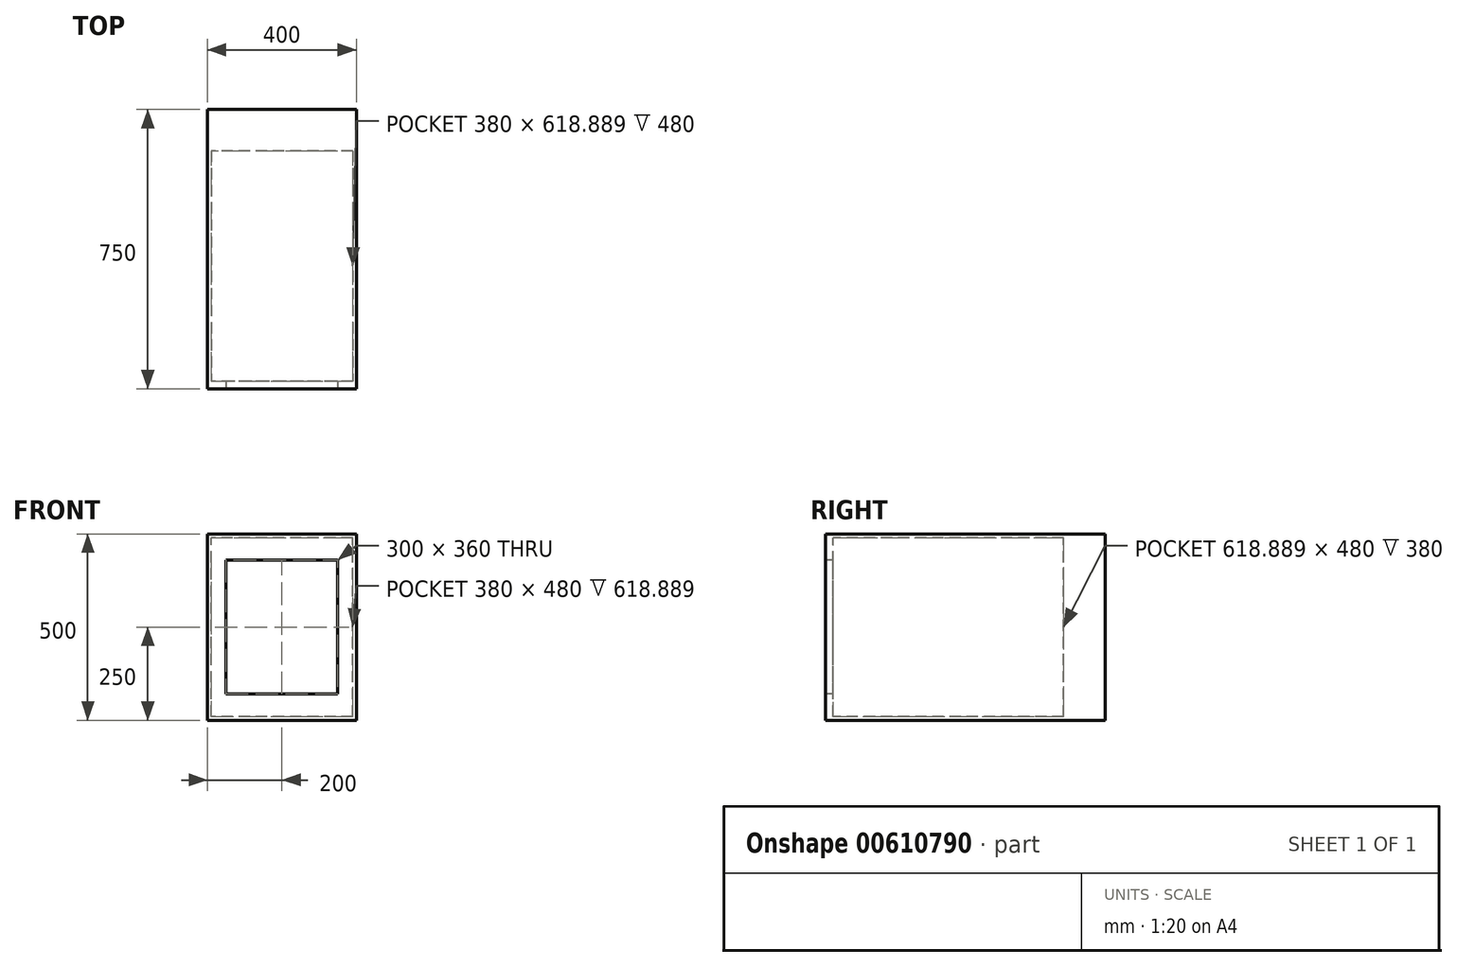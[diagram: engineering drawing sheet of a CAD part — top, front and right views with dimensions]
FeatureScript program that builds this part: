
annotation { "Feature Type Name" : "Feature", "Feature Type Description" : "" }
export const myFeature = defineFeature(function(context is Context, id is Id, definition is map)
    precondition{}
    {
        {
            var Q0;
            Q0=qCreatedBy(makeId("Front.planeOp"),FACE);
            var sketch = newSketch(context, id + "F0", { "sketchPlane" : qUnion([Q0])});
            skLineSegment(sketch, "E0.bottom", {"start": v(0, 0) * mm, "end": v(400, 0) * mm});
            skLineSegment(sketch, "E0.top", {"start": v(0, 500) * mm, "end": v(400, 500) * mm});
            skLineSegment(sketch, "E0.left", {"start": v(0, 0) * mm, "end": v(0, 500) * mm});
            skLineSegment(sketch, "E0.right", {"start": v(400, 0) * mm, "end": v(400, 500) * mm});
            skSolve(sketch);
        }
        {
            var Q0;
            Q0=qSketchRegion(id+"F0",true);
            extrude(context, id + "F1", {"entities" : qUnion([Q0]), "depth" : 750 * mm, "offsetDistance" : 25 * mm});
        }
        {
            var Q0;
            Q0=makeQuery(id+"F1.opExtrude","CAP_FACE",FACE,{"disambiguationData":[OSD([sQuery(id+"F0.wireOp",EDGE,"E0.bottom"),sQuery(id+"F0.wireOp",EDGE,"E0.top"),sQuery(id+"F0.wireOp",EDGE,"E0.left"),sQuery(id+"F0.wireOp",EDGE,"E0.right")])],"isStart":false});
            var sketch = newSketch(context, id + "F2", { "sketchPlane" : qUnion([Q0])});
            skLineSegment(sketch, "E1", {"start": v(0, 0) * mm, "end": v(400, 500) * mm});
            skLineSegment(sketch, "E2.bottom", {"start": v(350, 70) * mm, "end": v(50, 70) * mm});
            skLineSegment(sketch, "E2.top", {"start": v(350, 430) * mm, "end": v(50, 430) * mm});
            skLineSegment(sketch, "E2.left", {"start": v(350, 70) * mm, "end": v(350, 430) * mm});
            skLineSegment(sketch, "E2.right", {"start": v(50, 70) * mm, "end": v(50, 430) * mm});
            skPoint(sketch, "E2.middle", {"position": v(200, 250) * mm});
            skSolve(sketch);
        }
        {
            var Q0;
            Q0=qSketchRegion(id+"F2",true);
            extrude(context, id + "F3", {"entities" : qUnion([Q0]), "operationType" : NewBodyOperationType.REMOVE, "oppositeDirection" : true, "depth" : 20 * mm, "offsetDistance" : 25 * mm});
        }
        {
            var Q0;
            Q0=makeQuery(id+"F3.boolean.opBoolean","COPY",FACE,{"derivedFrom":makeQuery(id+"F3.opExtrude","CAP_FACE",FACE,{"disambiguationData":[OSD([sQuery(id+"F2.wireOp",EDGE,"E2.bottom"),sQuery(id+"F2.wireOp",EDGE,"E2.top"),sQuery(id+"F2.wireOp",EDGE,"E2.left"),sQuery(id+"F2.wireOp",EDGE,"E2.right")])],"isStart":false})});
            var sketch = newSketch(context, id + "F4", { "sketchPlane" : qUnion([Q0])});
            skLineSegment(sketch, "E3", {"start": v(50, 70) * mm, "end": v(350, 430) * mm});
            skLineSegment(sketch, "E4.bottom", {"start": v(390, 10) * mm, "end": v(10, 10) * mm});
            skLineSegment(sketch, "E4.top", {"start": v(390, 490) * mm, "end": v(10, 490) * mm});
            skLineSegment(sketch, "E4.left", {"start": v(390, 10) * mm, "end": v(390, 490) * mm});
            skLineSegment(sketch, "E4.right", {"start": v(10, 10) * mm, "end": v(10, 490) * mm});
            skPoint(sketch, "E4.middle", {"position": v(200, 250) * mm});
            skSolve(sketch);
        }
        {
            var Q0;
            Q0=qSketchRegion(id+"F4",true);
            extrude(context, id + "F5", {"entities" : qUnion([Q0]), "operationType" : NewBodyOperationType.REMOVE, "oppositeDirection" : true, "depth" : 618.9 * mm, "offsetDistance" : 25 * mm});
        }
    });
